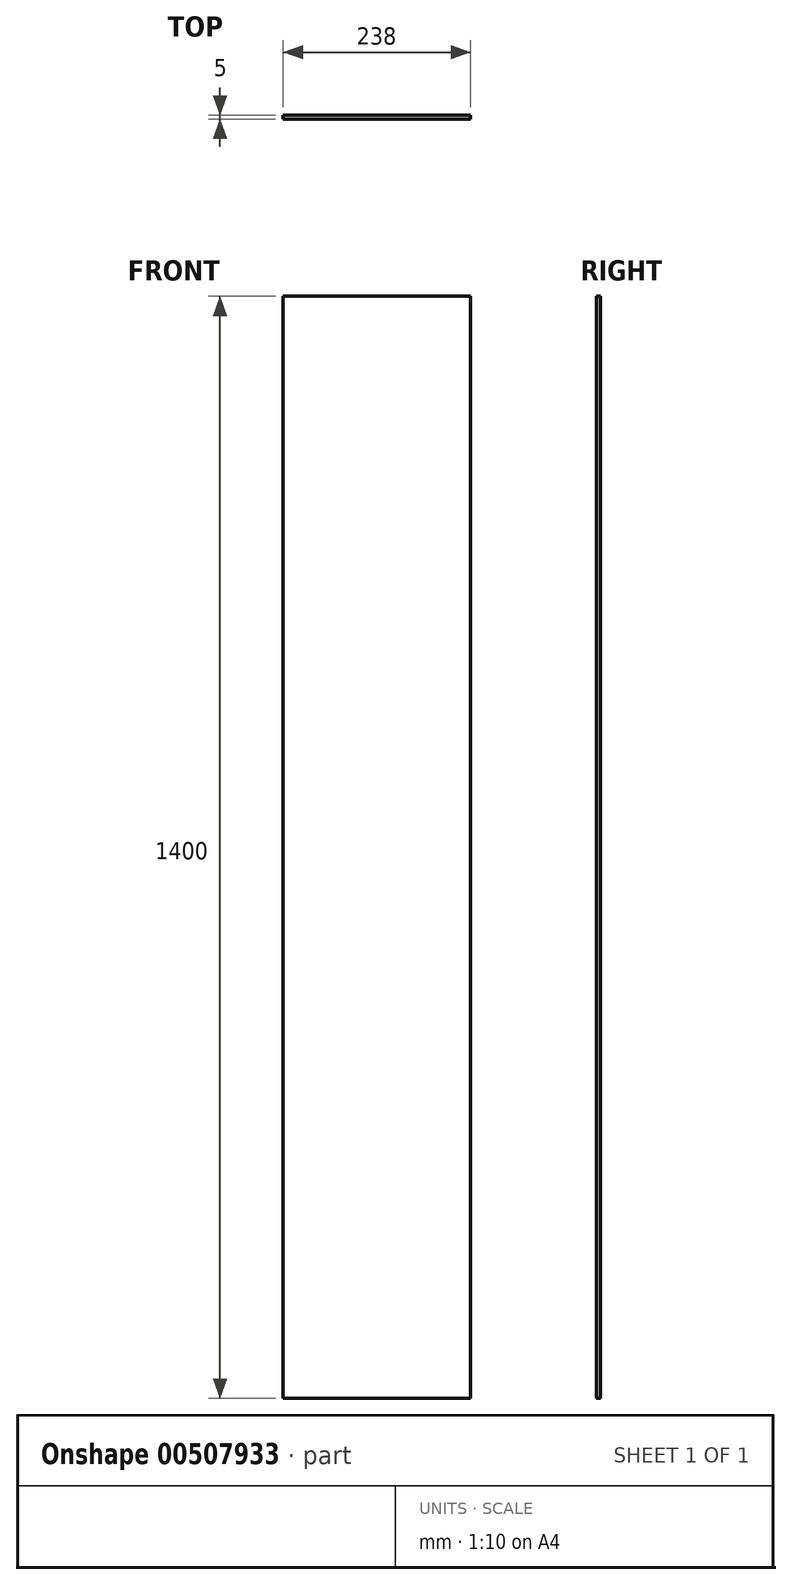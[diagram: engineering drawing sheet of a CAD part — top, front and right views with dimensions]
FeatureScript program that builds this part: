
annotation { "Feature Type Name" : "Feature", "Feature Type Description" : "" }
export const myFeature = defineFeature(function(context is Context, id is Id, definition is map)
    precondition{}
    {
        {
            var Q0;
            Q0=qCreatedBy(makeId("Top.planeOp"),FACE);
            var sketch = newSketch(context, id + "F0", { "sketchPlane" : qUnion([Q0])});
            skLineSegment(sketch, "E0.bottom", {"start": v(-119, 2.5) * mm, "end": v(119, 2.5) * mm});
            skLineSegment(sketch, "E0.top", {"start": v(-119, -2.5) * mm, "end": v(119, -2.5) * mm});
            skLineSegment(sketch, "E0.left", {"start": v(-119, 2.5) * mm, "end": v(-119, -2.5) * mm});
            skLineSegment(sketch, "E0.right", {"start": v(119, 2.5) * mm, "end": v(119, -2.5) * mm});
            skPoint(sketch, "E0.middle", {"position": v(0, 0) * mm});
            skSolve(sketch);
        }
        {
            var Q0;
            Q0 = qSketchRegion(id + "F0", true);
            extrude(context, id + "F1", {"entities" : qUnion([Q0]), "depth" : 1400 * mm, "offsetDistance" : 25 * mm});
        }
    });
